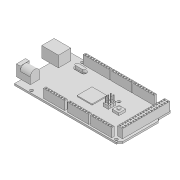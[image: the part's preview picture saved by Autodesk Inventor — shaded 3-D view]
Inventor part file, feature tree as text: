
AUTODESK INVENTOR PART (.ipt)
format: ipt  version: 2020 (Build 240168000, 168)  size: 414,720 bytes
history: native  units: mm
features: other x7, fillet x1
ambient origin geometry x8: Origin, YZ Plane, XZ Plane, XY Plane, X Axis, Y Axis, Z Axis, Center Point
bodies: Body1 (feature_tree), Body2 (feature_tree), Body3 (feature_tree), Body4 (feature_tree)
feature tree (8):
  other  "Sólido1"
  other  "Sólido2"
  other  "Sólido3"
  other  "Sólido4"
  other  "Cut-Extrude2"
  fillet  "Fillet1"  [1 undecoded]
  other  "Boss-Extrude4"
  other  "Boss-Extrude13"
note: 1 required parameter value undecoded (feature->parameter linkage not recoverable at this tier; creation-order binding heuristic only, values carry confidence <= 0.55)
